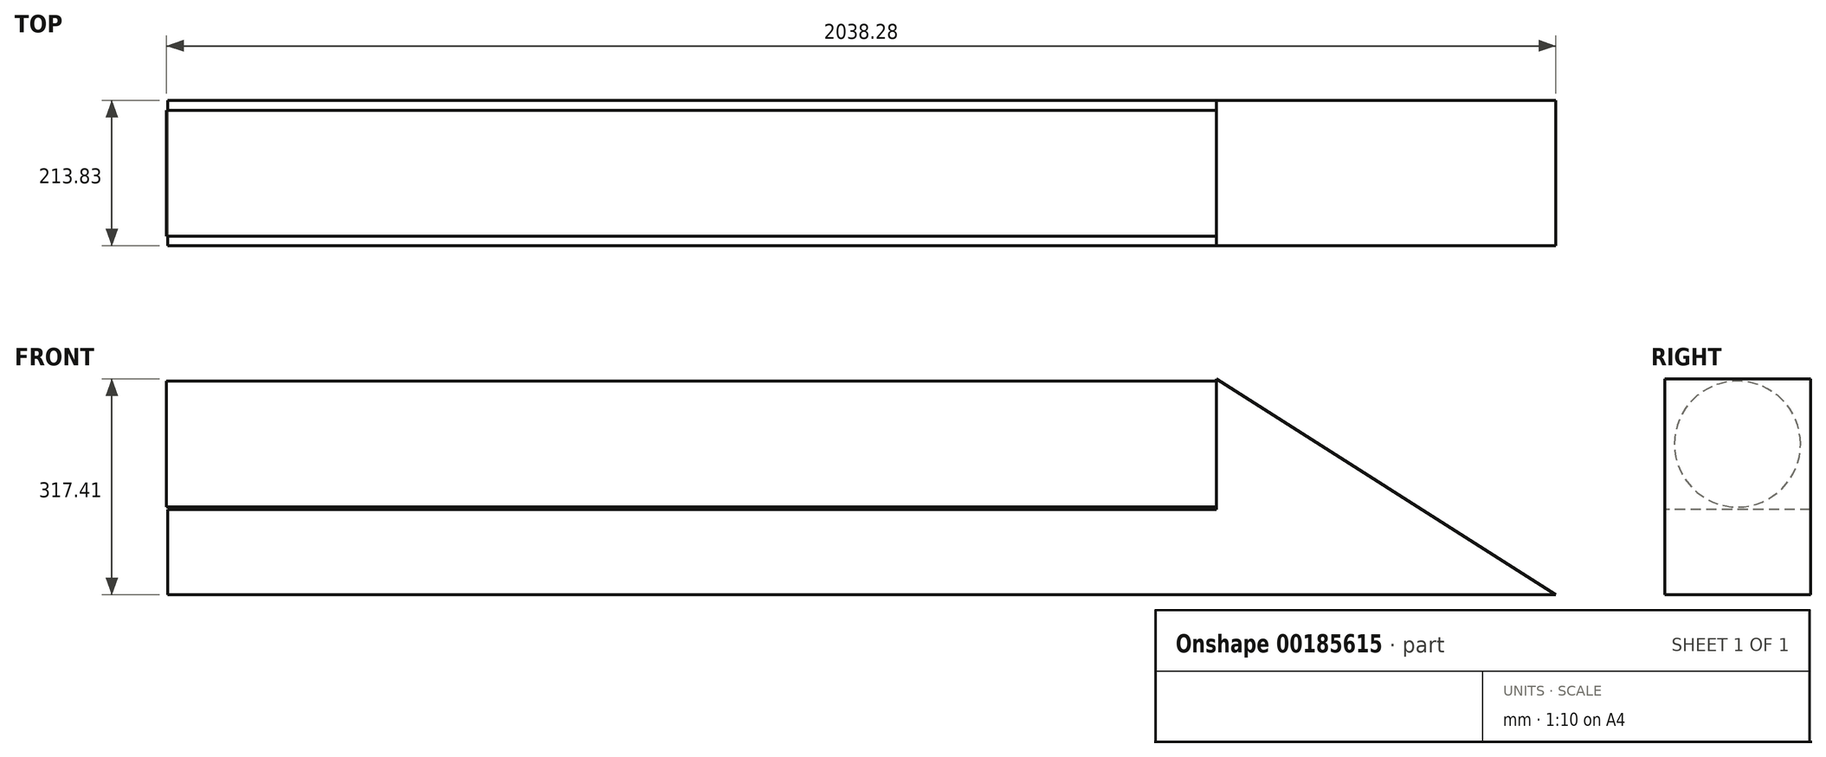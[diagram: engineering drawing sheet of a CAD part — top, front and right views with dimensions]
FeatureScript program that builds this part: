
annotation { "Feature Type Name" : "Feature", "Feature Type Description" : "" }
export const myFeature = defineFeature(function(context is Context, id is Id, definition is map)
    precondition{}
    {
        {
            var Q0;
            Q0=qCreatedBy(makeId("Front.planeOp"),FACE);
            var sketch = newSketch(context, id + "F0", { "sketchPlane" : qUnion([Q0])});
            skLineSegment(sketch, "E0", {"start": v(953.75, -238.27) * mm, "end": v(456.09, 79.14) * mm});
            skLineSegment(sketch, "E1", {"start": v(456.09, 79.14) * mm, "end": v(456.09, -112.87) * mm});
            skLineSegment(sketch, "E2", {"start": v(456.09, -112.87) * mm, "end": v(-378.57, -112.87) * mm});
            skLineSegment(sketch, "E3", {"start": v(-378.57, -112.87) * mm, "end": v(-378.57, -238.27) * mm});
            skLineSegment(sketch, "E4", {"start": v(-378.57, -238.27) * mm, "end": v(953.75, -238.27) * mm});
            skSolve(sketch);
        }
        {
            var Q0;
            Q0 = qSketchRegion(id + "F0", true);
            extrude(context, id + "F1", {"entities" : qUnion([Q0]), "oppositeDirection" : true, "depth" : 213.83 * mm});
        }
        {
            var Q0;
            Q0=makeQuery(id+"F1.opExtrude","SWEPT_FACE",FACE,{"disambiguationData":[OSD([sQuery(id+"F0.wireOp",EDGE,"E1")])]});
            var sketch = newSketch(context, id + "F2", { "sketchPlane" : qUnion([Q0])});
            skCircle(sketch, "E5", {"center": v(-106.64, -16.87) * mm, "radius": 92.44 * mm});
            skPoint(sketch, "E5.centerSnap0", {"position": v(0, -16.87) * mm});
            skSolve(sketch);
        }
        {
            var Q0;
            Q0 = qSketchRegion(id + "F2", true);
            extrude(context, id + "F3", {"entities" : qUnion([Q0]), "operationType" : NewBodyOperationType.ADD, "depth" : 834.07 * mm});
        }
        {
            var Q0;
            Q0=makeQuery(id+"F1.opExtrude","SWEPT_FACE",FACE,{"disambiguationData":[OSD([sQuery(id+"F0.wireOp",EDGE,"E3")])]});
            extrude(context, id + "F4", {"entities" : qUnion([Q0]), "operationType" : NewBodyOperationType.ADD, "depth" : 265.76 * mm});
        }
        {
            var Q0;
            Q0=makeQuery(id+"F3.opExtrude","CAP_FACE",FACE,{"disambiguationData":[OSD([sQuery(id+"F2.wireOp",EDGE,"E5")])],"isStart":false});
            extrude(context, id + "F5", {"entities" : qUnion([Q0]), "operationType" : NewBodyOperationType.ADD, "depth" : 264.64 * mm});
        }
        {
            var Q0;
            Q0=makeQuery(id+"F5.opExtrude","CAP_FACE",FACE,{"disambiguationData":[OSD([sQuery(id+"F2.wireOp",EDGE,"E5")])],"isStart":false});
            extrude(context, id + "F6", {"entities" : qUnion([Q0]), "operationType" : NewBodyOperationType.ADD, "depth" : 25.4 * mm});
        }
        {
            var Q0;
            Q0=makeQuery(id+"F6.opExtrude","CAP_FACE",FACE,{"disambiguationData":[OSD([sQuery(id+"F2.wireOp",EDGE,"E5")])],"isStart":false});
            var Q1;
            Q1=makeQuery(id+"F4.opExtrude","CAP_FACE",FACE,{"disambiguationData":[OSD([sQuery(id+"F0.wireOp",EDGE,"E3")])],"isStart":false});
            extrude(context, id + "F7", {"entities" : qUnion([Q0, Q1]), "operationType" : NewBodyOperationType.ADD, "depth" : 416.5 * mm});
        }
        {
            var Q0;
            Q0=makeQuery(id+"F7.opExtrude","CAP_FACE",FACE,{"disambiguationData":[OSD([sQuery(id+"F0.wireOp",EDGE,"E3")])],"isStart":false});
            extrude(context, id + "F8", {"entities" : qUnion([Q0]), "operationType" : NewBodyOperationType.ADD, "depth" : 22.02 * mm});
        }
    });
